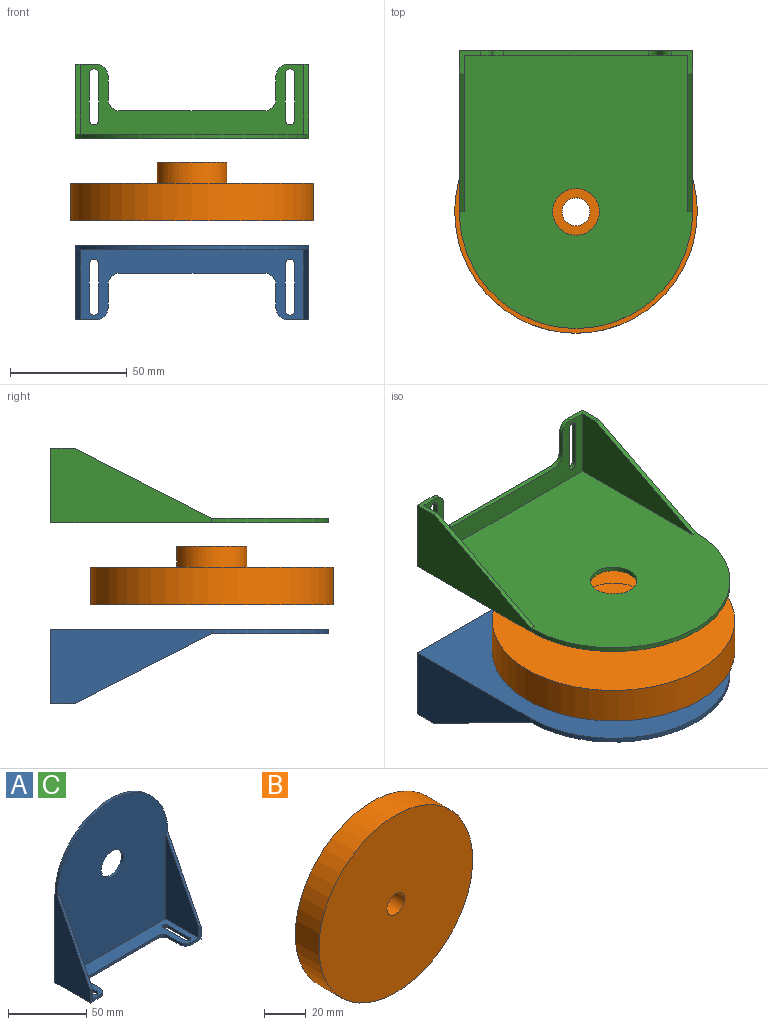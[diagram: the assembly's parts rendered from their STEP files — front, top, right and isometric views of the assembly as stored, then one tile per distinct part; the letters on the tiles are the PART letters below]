
ASSEMBLY  parts=3 mates=1
PART A: 29 faces, bbox 100x32x119 mm
  f0: plane 67x30mm, normal (-1,0,0), area 1125mm2, adj f1,f8,f9,f16
  f1: plane 117x100mm, normal (0,-1,0), area 10044.8mm2, adj f0,f3,f6,f8,f10,f12,f16
  f2: plane 69x32mm, normal (1,0,0), area 1323mm2, adj f3,f5,f7,f8,f9
  f3: cylinder r=50mm len=100mm, axis (0,1,0), area 314.2mm2, adj f1,f2,f4,f7
  f4: plane 69x32mm, normal (-1,0,0), area 1323mm2, adj f3,f5,f7,f10,f11
  f5: plane 100x32mm, normal (0,0,-1), area 1574.9mm2, adj f2,f4,f7,f9,f11,f13,f14,f15
  f6: cylinder r=10mm len=20mm, axis (0,1,0), area 125.7mm2, adj f1,f7
  f7: plane 119x100mm, normal (0,1,0), area 10512.8mm2, adj f2,f3,f4,f5,f6
  f8: plane 59x30mm, normal (0,-0.89,0.45), area 132.4mm2, adj f0,f1,f2,f9
  f9: plane 10x9mm, normal (0,-1,0), area 34mm2, adj f0,f2,f5,f8,f16,f17
  f10: plane 59x30mm, normal (0,-0.89,0.45), area 132.4mm2, adj f1,f4,f11,f12
  f11: plane 10x9mm, normal (0,-1,0), area 34mm2, adj f4,f5,f10,f12,f16,f18
  f12: plane 67x30mm, normal (1,0,0), area 1125mm2, adj f1,f10,f11,f16
  f13: plane 10x2mm, normal (-1,0,0), area 20mm2, adj f5,f16,f17,f20
  f14: plane 62x2mm, normal (0,-1,0), area 124mm2, adj f5,f16,f19,f20
  f15: plane 10x2mm, normal (1,0,0), area 20mm2, adj f5,f16,f18,f19
  f16: plane 96x30mm, normal (0,0,1), area 1254.9mm2, adj f0,f1,f9,f11,f12,f13,f14,f15
  f17: cylinder r=5mm len=5mm, axis (0,0,-1), area 15.7mm2, adj f5,f9,f13,f16
  f18: cylinder r=5mm len=5mm, axis (0,0,1), area 15.7mm2, adj f5,f11,f15,f16
  f19: cylinder r=5mm len=5mm, axis (0,0,-1), area 15.7mm2, adj f5,f14,f15,f16
  f20: cylinder r=5mm len=5mm, axis (0,0,1), area 15.7mm2, adj f5,f13,f14,f16
  f21: plane 20x2mm, normal (1,0,0), area 40mm2, adj f5,f16,f22,f24
  f22: cylinder r=2mm len=4mm, axis (0,0,1), area 12.6mm2, adj f5,f16,f21,f23
  f23: plane 20x2mm, normal (-1,0,0), area 40mm2, adj f5,f16,f22,f24
  f24: cylinder r=2mm len=4mm, axis (0,0,1), area 12.6mm2, adj f5,f16,f21,f23
  f25: plane 20x2mm, normal (-1,0,0), area 40mm2, adj f5,f16,f26,f28
  f26: cylinder r=2mm len=4mm, axis (0,0,1), area 12.6mm2, adj f5,f16,f25,f27
  f27: plane 20x2mm, normal (1,0,0), area 40mm2, adj f5,f16,f26,f28
  f28: cylinder r=2mm len=4mm, axis (0,0,1), area 12.6mm2, adj f5,f16,f25,f27
PART B: 78 faces, bbox 104x25x104 mm
  f0: plane 20x2.89mm, normal (-0.61,-0.79,0), area 72.9mm2, adj f1,f3,f4,f8
  f1: cylinder r=5.25mm len=25mm, axis (0,0,1), area 604.8mm2, adj f0,f2,f4,f5,f6,f7,f8
  f2: plane 20x2.89mm, normal (0.61,-0.79,0), area 72.9mm2, adj f1,f3,f4,f8
  f3: cylinder r=0.5mm len=20mm, axis (0,0,1), area 13.1mm2, adj f0,f2,f4,f8
  f4: plane 11.74x10.5mm, normal (0,0,1), area 89.7mm2, adj f0,f1,f2,f3
  f5: plane 14.25x10.5mm, normal (0,0,-1), area 137.8mm2, adj f1,f6,f7,f12
  f6: plane 9x5mm, normal (-1,0,0), area 45mm2, adj f1,f5,f8,f12
  f7: plane 9x5mm, normal (1,0,0), area 45mm2, adj f1,f5,f8,f12
  f8: plane 10.5x9mm, normal (0,0,1), area 48.1mm2, adj f0,f1,f2,f3,f6,f7,f12
  f9: plane 30x30mm, normal (0,1,0), area 593.8mm2, adj f13,f14
  f10: plane 104x104mm, normal (0,-1,0), area 8381.8mm2, adj f11,f14
  f11: cylinder r=52mm len=104mm, axis (0,-1,0), area 5227.6mm2, adj f10,f12
  f12: plane 104x104mm, normal (0,1,0), area 7368mm2, adj f5,f6,f7,f8,f11,f13,f15,f16
  f13: cylinder r=15mm len=30mm, axis (0,-1,0), area 848.2mm2, adj f9,f12
  f14: cylinder r=6mm len=25mm, axis (0,1,0), area 942.5mm2, adj f9,f10
  f15: plane 9x5mm, normal (1,0,0), area 45mm2, adj f12,f17,f37,f41
  f16: plane 9x5mm, normal (-1,0,0), area 45mm2, adj f12,f17,f37,f41
  f17: plane 10.5x9mm, normal (0,0,-1), area 48.1mm2, adj f12,f15,f16,f36,f37,f38,f39
  f18: plane 9x3.54mm, normal (0.71,0,0.71), area 45mm2, adj f12,f20,f43,f47
  f19: plane 9x3.54mm, normal (-0.71,0,-0.71), area 45mm2, adj f12,f20,f43,f47
  f20: plane 9x7.42mm, normal (0.71,0,-0.71), area 48.1mm2, adj f12,f18,f19,f42,f43,f44,f45
  f21: plane 9x5mm, normal (0,0,1), area 45mm2, adj f12,f23,f49,f53
  f22: plane 9x5mm, normal (0,0,-1), area 45mm2, adj f12,f23,f49,f53
  f23: plane 10.5x9mm, normal (1,0,0), area 48.1mm2, adj f12,f21,f22,f48,f49,f50,f51
  f24: plane 9x3.54mm, normal (-0.71,0,0.71), area 45mm2, adj f12,f26,f55,f59
  f25: plane 9x3.54mm, normal (0.71,0,-0.71), area 45mm2, adj f12,f26,f55,f59
  f26: plane 9x7.42mm, normal (0.71,0,0.71), area 48.1mm2, adj f12,f24,f25,f54,f55,f56,f57
  f27: plane 9x3.54mm, normal (-0.71,0,-0.71), area 45mm2, adj f12,f29,f61,f65
  f28: plane 9x3.54mm, normal (0.71,0,0.71), area 45mm2, adj f12,f29,f61,f65
  f29: plane 9x7.42mm, normal (-0.71,0,0.71), area 48.1mm2, adj f12,f27,f28,f60,f61,f62,f63
  f30: plane 9x5mm, normal (0,0,-1), area 45mm2, adj f12,f32,f67,f71
  f31: plane 9x5mm, normal (0,0,1), area 45mm2, adj f12,f32,f67,f71
  f32: plane 10.5x9mm, normal (-1,0,0), area 48.1mm2, adj f12,f30,f31,f66,f67,f68,f69
  f33: plane 9x3.54mm, normal (0.71,0,-0.71), area 45mm2, adj f12,f35,f73,f77
  f34: plane 9x3.54mm, normal (-0.71,0,0.71), area 45mm2, adj f12,f35,f73,f77
  f35: plane 9x7.42mm, normal (-0.71,0,-0.71), area 48.1mm2, adj f12,f33,f34,f72,f73,f74,f75
  f36: plane 20x2.89mm, normal (0.61,-0.79,0), area 72.9mm2, adj f17,f37,f39,f40
  f37: cylinder r=5.25mm len=25mm, axis (0,0,-1), area 604.8mm2, adj f15,f16,f17,f36,f38,f40,f41
  f38: plane 20x2.89mm, normal (-0.61,-0.79,0), area 72.9mm2, adj f17,f37,f39,f40
  f39: cylinder r=0.5mm len=20mm, axis (0,0,-1), area 13.1mm2, adj f17,f36,f38,f40
  f40: plane 11.74x10.5mm, normal (0,0,-1), area 89.7mm2, adj f36,f37,f38,f39
  f41: plane 14.25x10.5mm, normal (0,0,1), area 137.8mm2, adj f12,f15,f16,f37
  f42: plane 16.19x16.19mm, normal (0.43,-0.79,0.43), area 72.9mm2, adj f20,f43,f45,f46
  f43: cylinder r=5.25mm len=25.1mm, axis (0.71,0,-0.71), area 604.8mm2, adj f18,f19,f20,f42,f44,f46,f47
  f44: plane 16.19x16.19mm, normal (-0.43,-0.79,-0.43), area 72.9mm2, adj f20,f43,f45,f46
  f45: cylinder r=0.5mm len=14.57mm, axis (0.71,0,-0.71), area 13.1mm2, adj f20,f42,f44,f46
  f46: plane 11.74x7.42mm, normal (0.71,0,-0.71), area 89.7mm2, adj f42,f43,f44,f45
  f47: plane 14.25x7.42mm, normal (-0.71,0,0.71), area 137.8mm2, adj f12,f18,f19,f43
  f48: plane 20x2.89mm, normal (0,-0.79,0.61), area 72.9mm2, adj f23,f49,f51,f52
  f49: cylinder r=5.25mm len=25mm, axis (1,0,0), area 604.8mm2, adj f21,f22,f23,f48,f50,f52,f53
  f50: plane 20x2.89mm, normal (0,-0.79,-0.61), area 72.9mm2, adj f23,f49,f51,f52
  f51: cylinder r=0.5mm len=20mm, axis (1,0,0), area 13.1mm2, adj f23,f48,f50,f52
  f52: plane 11.74x10.5mm, normal (1,0,0), area 89.7mm2, adj f48,f49,f50,f51
  f53: plane 14.25x10.5mm, normal (-1,0,0), area 137.8mm2, adj f12,f21,f22,f49
  f54: plane 16.19x16.19mm, normal (-0.43,-0.79,0.43), area 72.9mm2, adj f26,f55,f57,f58
  f55: cylinder r=5.25mm len=25.1mm, axis (0.71,0,0.71), area 604.8mm2, adj f24,f25,f26,f54,f56,f58,f59
  f56: plane 16.19x16.19mm, normal (0.43,-0.79,-0.43), area 72.9mm2, adj f26,f55,f57,f58
  f57: cylinder r=0.5mm len=14.57mm, axis (0.71,0,0.71), area 13.1mm2, adj f26,f54,f56,f58
  f58: plane 11.74x7.42mm, normal (0.71,0,0.71), area 89.7mm2, adj f54,f55,f56,f57
  f59: plane 14.25x7.42mm, normal (-0.71,0,-0.71), area 137.8mm2, adj f12,f24,f25,f55
  f60: plane 16.19x16.19mm, normal (-0.43,-0.79,-0.43), area 72.9mm2, adj f29,f61,f63,f64
  f61: cylinder r=5.25mm len=25.1mm, axis (-0.71,0,0.71), area 604.8mm2, adj f27,f28,f29,f60,f62,f64,f65
  f62: plane 16.19x16.19mm, normal (0.43,-0.79,0.43), area 72.9mm2, adj f29,f61,f63,f64
  f63: cylinder r=0.5mm len=14.57mm, axis (-0.71,0,0.71), area 13.1mm2, adj f29,f60,f62,f64
  f64: plane 11.74x7.42mm, normal (-0.71,0,0.71), area 89.7mm2, adj f60,f61,f62,f63
  f65: plane 14.25x7.42mm, normal (0.71,0,-0.71), area 137.8mm2, adj f12,f27,f28,f61
  f66: plane 20x2.89mm, normal (0,-0.79,-0.61), area 72.9mm2, adj f32,f67,f69,f70
  f67: cylinder r=5.25mm len=25mm, axis (-1,0,0), area 604.8mm2, adj f30,f31,f32,f66,f68,f70,f71
  f68: plane 20x2.89mm, normal (0,-0.79,0.61), area 72.9mm2, adj f32,f67,f69,f70
  f69: cylinder r=0.5mm len=20mm, axis (-1,0,0), area 13.1mm2, adj f32,f66,f68,f70
  f70: plane 11.74x10.5mm, normal (-1,0,0), area 89.7mm2, adj f66,f67,f68,f69
  f71: plane 14.25x10.5mm, normal (1,0,0), area 137.8mm2, adj f12,f30,f31,f67
  f72: plane 16.19x16.19mm, normal (0.43,-0.79,-0.43), area 72.9mm2, adj f35,f73,f75,f76
  f73: cylinder r=5.25mm len=25.1mm, axis (-0.71,0,-0.71), area 604.8mm2, adj f33,f34,f35,f72,f74,f76,f77
  f74: plane 16.19x16.19mm, normal (-0.43,-0.79,0.43), area 72.9mm2, adj f35,f73,f75,f76
  f75: cylinder r=0.5mm len=14.57mm, axis (-0.71,0,-0.71), area 13.1mm2, adj f35,f72,f74,f76
  f76: plane 11.74x7.42mm, normal (-0.71,0,-0.71), area 89.7mm2, adj f72,f73,f74,f75
  f77: plane 14.25x7.42mm, normal (0.71,0,0.71), area 137.8mm2, adj f12,f33,f34,f73
PART C: same geometry as A
PLACE A rot(axis=(1,0,0),90deg) t=(0,0,-35.5)mm
PLACE B rot(axis=(0,-0.71,-0.71),180deg) t=(0,0,-25)mm
PLACE C rot(axis=(0,-0.71,0.71),180deg) t=(0,0,10)mm
MATE fastened B.f11 <-> A.f6  axis (0,0,1) through (0,0,-12.5)mm
